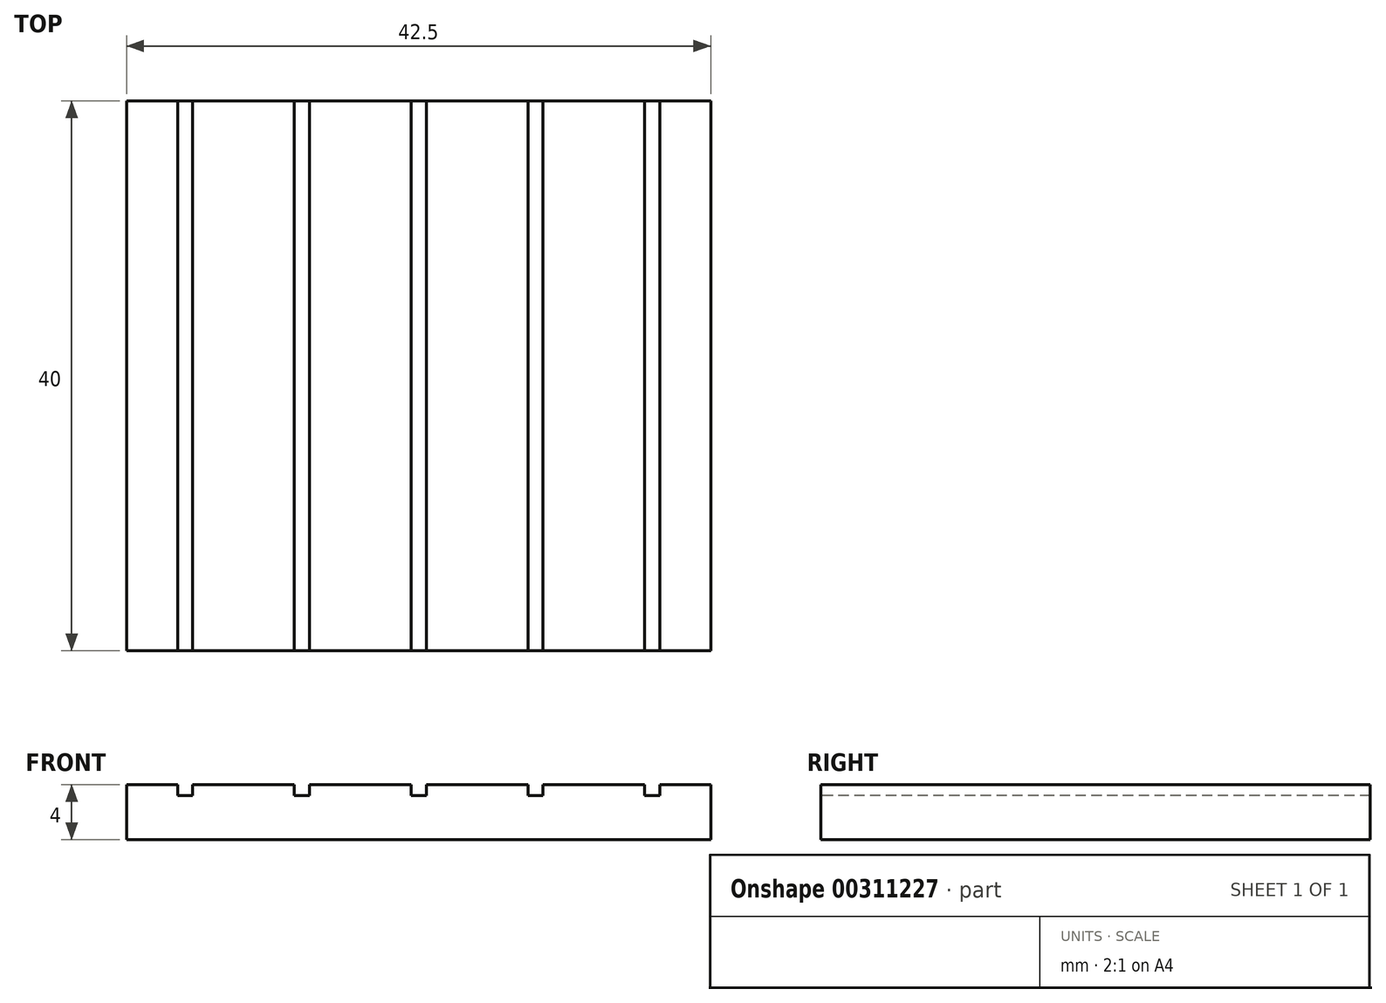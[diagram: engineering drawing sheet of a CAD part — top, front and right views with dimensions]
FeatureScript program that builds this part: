
annotation { "Feature Type Name" : "Feature", "Feature Type Description" : "" }
export const myFeature = defineFeature(function(context is Context, id is Id, definition is map)
    precondition{}
    {
        {
            var Q0;
            Q0=qCreatedBy(makeId("Front.planeOp"),FACE);
            var sketch = newSketch(context, id + "F0", { "sketchPlane" : qUnion([Q0])});
            skLineSegment(sketch, "E0.bottom", {"start": v(0, 0) * mm, "end": v(8.5, 0) * mm});
            skLineSegment(sketch, "E0.top", {"start": v(0, 4) * mm, "end": v(3.7, 4) * mm});
            skLineSegment(sketch, "E0.left", {"start": v(0, 0) * mm, "end": v(0, 4) * mm});
            skLineSegment(sketch, "E0.right", {"start": v(8.5, 0) * mm, "end": v(8.5, 4) * mm});
            skLineSegment(sketch, "E1", {"start": v(4.25, 4) * mm, "end": v(4.25, 0) * mm, "construction": true});
            skLineSegment(sketch, "E2", {"start": v(3.7, 4) * mm, "end": v(3.7, 3.2) * mm});
            skLineSegment(sketch, "E3", {"start": v(3.7, 3.2) * mm, "end": v(4.8, 3.2) * mm});
            skLineSegment(sketch, "E4", {"start": v(4.8, 3.2) * mm, "end": v(4.8, 4) * mm});
            skLineSegment(sketch, "E5.trimOffspring", {"start": v(4.8, 4) * mm, "end": v(8.5, 4) * mm});
            skLineSegment(sketch, "E6.1.0.0", {"start": v(12.2, 3.2) * mm, "end": v(13.3, 3.2) * mm});
            skLineSegment(sketch, "E6.1.0.1", {"start": v(17, 0) * mm, "end": v(17, 4) * mm});
            skLineSegment(sketch, "E6.1.0.2", {"start": v(8.5, 4) * mm, "end": v(12.2, 4) * mm});
            skLineSegment(sketch, "E6.1.0.3", {"start": v(13.3, 3.2) * mm, "end": v(13.3, 4) * mm});
            skLineSegment(sketch, "E6.1.0.4", {"start": v(12.2, 4) * mm, "end": v(12.2, 3.2) * mm});
            skLineSegment(sketch, "E6.1.0.5", {"start": v(8.5, 0) * mm, "end": v(17, 0) * mm});
            skLineSegment(sketch, "E6.1.0.6", {"start": v(12.75, 4) * mm, "end": v(12.75, 0) * mm, "construction": true});
            skLineSegment(sketch, "E6.1.0.7", {"start": v(13.3, 4) * mm, "end": v(17, 4) * mm});
            skLineSegment(sketch, "E6.2.0.0", {"start": v(20.7, 3.2) * mm, "end": v(21.8, 3.2) * mm});
            skLineSegment(sketch, "E6.2.0.1", {"start": v(25.5, 0) * mm, "end": v(25.5, 4) * mm});
            skLineSegment(sketch, "E6.2.0.2", {"start": v(17, 4) * mm, "end": v(20.7, 4) * mm});
            skLineSegment(sketch, "E6.2.0.3", {"start": v(21.8, 3.2) * mm, "end": v(21.8, 4) * mm});
            skLineSegment(sketch, "E6.2.0.4", {"start": v(20.7, 4) * mm, "end": v(20.7, 3.2) * mm});
            skLineSegment(sketch, "E6.2.0.5", {"start": v(17, 0) * mm, "end": v(25.5, 0) * mm});
            skLineSegment(sketch, "E6.2.0.6", {"start": v(21.25, 4) * mm, "end": v(21.25, 0) * mm, "construction": true});
            skLineSegment(sketch, "E6.2.0.7", {"start": v(21.8, 4) * mm, "end": v(25.5, 4) * mm});
            skLineSegment(sketch, "E6.2.0.8", {"start": v(17, 0) * mm, "end": v(17, 4) * mm});
            skLineSegment(sketch, "E6.3.0.0", {"start": v(29.2, 3.2) * mm, "end": v(30.3, 3.2) * mm});
            skLineSegment(sketch, "E6.3.0.1", {"start": v(34, 0) * mm, "end": v(34, 4) * mm});
            skLineSegment(sketch, "E6.3.0.2", {"start": v(25.5, 4) * mm, "end": v(29.2, 4) * mm});
            skLineSegment(sketch, "E6.3.0.3", {"start": v(30.3, 3.2) * mm, "end": v(30.3, 4) * mm});
            skLineSegment(sketch, "E6.3.0.4", {"start": v(29.2, 4) * mm, "end": v(29.2, 3.2) * mm});
            skLineSegment(sketch, "E6.3.0.5", {"start": v(25.5, 0) * mm, "end": v(34, 0) * mm});
            skLineSegment(sketch, "E6.3.0.6", {"start": v(29.75, 4) * mm, "end": v(29.75, 0) * mm, "construction": true});
            skLineSegment(sketch, "E6.3.0.7", {"start": v(30.3, 4) * mm, "end": v(34, 4) * mm});
            skLineSegment(sketch, "E6.3.0.8", {"start": v(25.5, 0) * mm, "end": v(25.5, 4) * mm});
            skLineSegment(sketch, "E6.4.0.0", {"start": v(37.7, 3.2) * mm, "end": v(38.8, 3.2) * mm});
            skLineSegment(sketch, "E6.4.0.1", {"start": v(42.5, 0) * mm, "end": v(42.5, 4) * mm});
            skLineSegment(sketch, "E6.4.0.2", {"start": v(34, 4) * mm, "end": v(37.7, 4) * mm});
            skLineSegment(sketch, "E6.4.0.3", {"start": v(38.8, 3.2) * mm, "end": v(38.8, 4) * mm});
            skLineSegment(sketch, "E6.4.0.4", {"start": v(37.7, 4) * mm, "end": v(37.7, 3.2) * mm});
            skLineSegment(sketch, "E6.4.0.5", {"start": v(34, 0) * mm, "end": v(42.5, 0) * mm});
            skLineSegment(sketch, "E6.4.0.6", {"start": v(38.25, 4) * mm, "end": v(38.25, 0) * mm, "construction": true});
            skLineSegment(sketch, "E6.4.0.7", {"start": v(38.8, 4) * mm, "end": v(42.5, 4) * mm});
            skLineSegment(sketch, "E6.4.0.8", {"start": v(34, 0) * mm, "end": v(34, 4) * mm});
            skLineSegment(sketch, "E6.direction1", {"start": v(0, 0) * mm, "end": v(8.5, 0) * mm, "construction": true});
            skSolve(sketch);
        }
        {
            var Q0;
            Q0=makeQuery(id+"F0.imprint","IMPRINT",FACE,{"disambiguationData":[TD([[makeQuery(id+"F0.imprint","IMPRINT",EDGE,{"derivedFrom":sQuery(id+"F0.wireOp",EDGE,"E0.bottom")}),1.0]])]});
            var Q1;
            Q1=makeQuery(id+"F0.imprint","IMPRINT",FACE,{"disambiguationData":[TD([[makeQuery(id+"F0.imprint","IMPRINT",EDGE,{"derivedFrom":sQuery(id+"F0.wireOp",EDGE,"E6.1.0.0")}),-1.0]])]});
            var Q2;
            Q2=makeQuery(id+"F0.imprint","IMPRINT",FACE,{"disambiguationData":[TD([[makeQuery(id+"F0.imprint","IMPRINT",EDGE,{"derivedFrom":sQuery(id+"F0.wireOp",EDGE,"E6.2.0.0")}),-1.0]])]});
            var Q3;
            Q3=makeQuery(id+"F0.imprint","IMPRINT",FACE,{"disambiguationData":[TD([[makeQuery(id+"F0.imprint","IMPRINT",EDGE,{"derivedFrom":sQuery(id+"F0.wireOp",EDGE,"E6.3.0.0")}),-1.0]])]});
            var Q4;
            Q4=makeQuery(id+"F0.imprint","IMPRINT",FACE,{"disambiguationData":[TD([[makeQuery(id+"F0.imprint","IMPRINT",EDGE,{"derivedFrom":sQuery(id+"F0.wireOp",EDGE,"E6.4.0.0")}),-1.0]])]});
            extrude(context, id + "F1", {"entities" : qUnion([Q0, Q1, Q2, Q3, Q4]), "oppositeDirection" : true, "depth" : 40 * mm, "offsetDistance" : 25 * mm});
        }
    });
